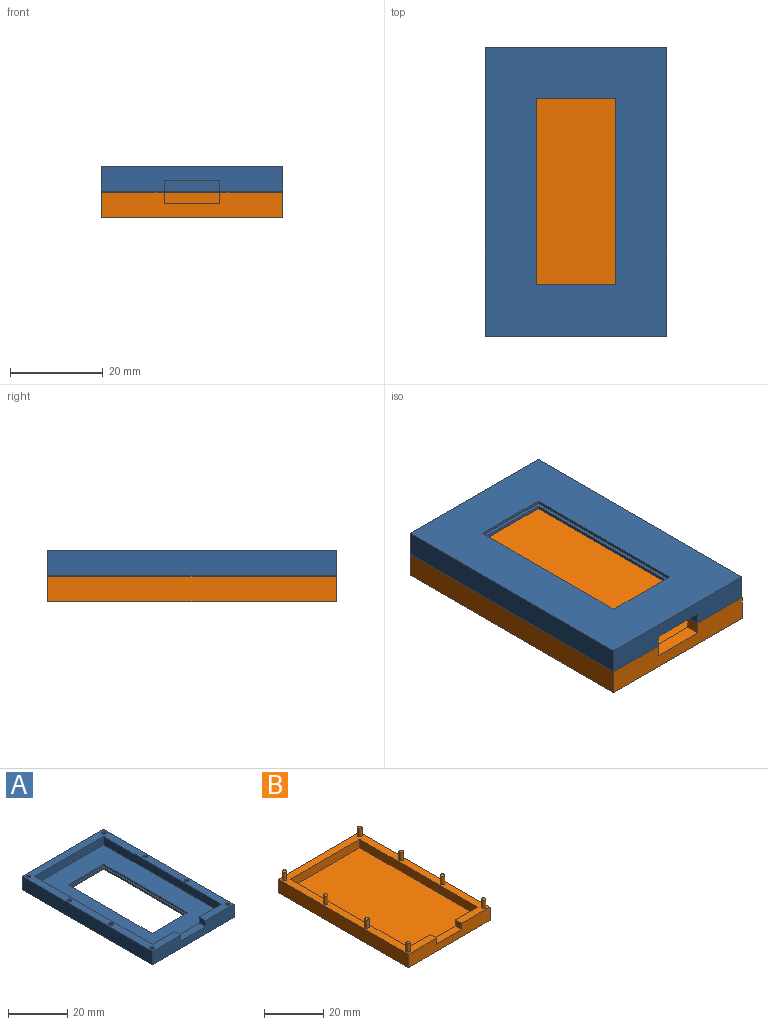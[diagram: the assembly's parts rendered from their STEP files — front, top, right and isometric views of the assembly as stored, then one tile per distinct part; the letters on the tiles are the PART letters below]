
ASSEMBLY  parts=2 mates=1
PART A: 44 faces, bbox 39x62x5.5 mm
  f0: plane 21x0.67mm, normal (0,-1,0), area 14mm2, adj f1,f3,f38,f43
  f1: plane 44x0.67mm, normal (-1,0,0), area 29.3mm2, adj f0,f2,f38,f43
  f2: plane 21x0.67mm, normal (0,1,0), area 14mm2, adj f1,f3,f38,f43
  f3: plane 44x0.67mm, normal (1,0,0), area 29.3mm2, adj f0,f2,f38,f43
  f4: plane 56x33mm, normal (0,0,1), area 1168mm2, adj f6,f7,f8,f9,f39,f40,f41,f42
  f5: plane 62x39mm, normal (0,0,-1), area 1738mm2, adj f12,f13,f14,f15,f34,f35,f36,f37
  f6: plane 33x3.5mm, normal (0,1,0), area 85.5mm2, adj f4,f7,f9,f10,f11,f16,f17
  f7: plane 56x3.5mm, normal (-1,0,0), area 196mm2, adj f4,f6,f8,f16
  f8: plane 33x3.5mm, normal (0,-1,0), area 115.5mm2, adj f4,f7,f9,f16
  f9: plane 56x3.5mm, normal (1,0,0), area 196mm2, adj f4,f6,f8,f16
  f10: plane 3x2.5mm, normal (1,0,0), area 7.5mm2, adj f6,f12,f16,f17
  f11: plane 3x2.5mm, normal (-1,0,0), area 7.5mm2, adj f6,f12,f16,f17
  f12: plane 39x5.5mm, normal (0,-1,0), area 184.5mm2, adj f5,f10,f11,f13,f15,f16,f17
  f13: plane 62x5.5mm, normal (1,0,0), area 341mm2, adj f5,f12,f14,f16
  f14: plane 39x5.5mm, normal (0,1,0), area 214.5mm2, adj f5,f13,f15,f16
  f15: plane 62x5.5mm, normal (-1,0,0), area 341mm2, adj f5,f12,f14,f16
  f16: plane 62x39mm, normal (0,0,1), area 519.9mm2, adj f6,f7,f8,f9,f10,f11,f12,f13
  f17: plane 12x3mm, normal (0,0,1), area 36mm2, adj f6,f10,f11,f12
  f18: cylinder r=0.75mm len=3.35mm, axis (0,0,1), area 15.8mm2, adj f16,f19
  f19: plane 1.5x1.5mm, normal (0,0,1), area 1.8mm2, adj f18
  f20: cylinder r=0.75mm len=3.35mm, axis (0,0,1), area 15.8mm2, adj f16,f21
  f21: plane 1.5x1.5mm, normal (0,0,1), area 1.8mm2, adj f20
  f22: cylinder r=0.75mm len=3.35mm, axis (0,0,1), area 15.8mm2, adj f16,f23
  f23: plane 1.5x1.5mm, normal (0,0,1), area 1.8mm2, adj f22
  f24: cylinder r=0.75mm len=3.35mm, axis (0,0,1), area 15.8mm2, adj f16,f25
  f25: plane 1.5x1.5mm, normal (0,0,1), area 1.8mm2, adj f24
  f26: cylinder r=0.75mm len=3.35mm, axis (0,0,1), area 15.8mm2, adj f16,f27
  f27: plane 1.5x1.5mm, normal (0,0,1), area 1.8mm2, adj f26
  f28: cylinder r=0.75mm len=3.35mm, axis (0,0,1), area 15.8mm2, adj f16,f29
  f29: plane 1.5x1.5mm, normal (0,0,1), area 1.8mm2, adj f28
  f30: cylinder r=0.75mm len=3.35mm, axis (0,0,1), area 15.8mm2, adj f16,f31
  f31: plane 1.5x1.5mm, normal (0,0,1), area 1.8mm2, adj f30
  f32: cylinder r=0.75mm len=3.35mm, axis (0,0,1), area 15.8mm2, adj f16,f33
  f33: plane 1.5x1.5mm, normal (0,0,1), area 1.8mm2, adj f32
  f34: plane 17x0.67mm, normal (0,-1,0), area 11.3mm2, adj f5,f35,f37,f38
  f35: plane 40x0.67mm, normal (-1,0,0), area 26.7mm2, adj f5,f34,f36,f38
  f36: plane 17x0.67mm, normal (0,1,0), area 11.3mm2, adj f5,f35,f37,f38
  f37: plane 40x0.67mm, normal (1,0,0), area 26.7mm2, adj f5,f34,f36,f38
  f38: plane 44x21mm, normal (0,0,1), area 244mm2, adj f0,f1,f2,f3,f34,f35,f36,f37
  f39: plane 17x0.67mm, normal (0,-1,0), area 11.3mm2, adj f4,f40,f42,f43
  f40: plane 40x0.67mm, normal (-1,0,0), area 26.7mm2, adj f4,f39,f41,f43
  f41: plane 17x0.67mm, normal (0,1,0), area 11.3mm2, adj f4,f40,f42,f43
  f42: plane 40x0.67mm, normal (1,0,0), area 26.7mm2, adj f4,f39,f41,f43
  f43: plane 44x21mm, normal (0,0,-1), area 244mm2, adj f0,f1,f2,f3,f39,f40,f41,f42
PART B: 30 faces, bbox 39x62x8.9 mm
  f0: plane 56x33mm, normal (0,0,1), area 1848mm2, adj f2,f3,f4,f5
  f1: plane 62x39mm, normal (0,0,-1), area 2418mm2, adj f8,f9,f10,f11
  f2: plane 33x3.5mm, normal (0,1,0), area 85.5mm2, adj f0,f3,f5,f6,f7,f12,f13
  f3: plane 56x3.5mm, normal (-1,0,0), area 196mm2, adj f0,f2,f4,f12
  f4: plane 33x3.5mm, normal (0,-1,0), area 115.5mm2, adj f0,f3,f5,f12
  f5: plane 56x3.5mm, normal (1,0,0), area 196mm2, adj f0,f2,f4,f12
  f6: plane 3x2.5mm, normal (1,0,0), area 7.5mm2, adj f2,f8,f12,f13
  f7: plane 3x2.5mm, normal (-1,0,0), area 7.5mm2, adj f2,f8,f12,f13
  f8: plane 39x5.5mm, normal (0,-1,0), area 184.5mm2, adj f1,f6,f7,f9,f11,f12,f13
  f9: plane 62x5.5mm, normal (1,0,0), area 341mm2, adj f1,f8,f10,f12
  f10: plane 39x5.5mm, normal (0,1,0), area 214.5mm2, adj f1,f9,f11,f12
  f11: plane 62x5.5mm, normal (-1,0,0), area 341mm2, adj f1,f8,f10,f12
  f12: plane 62x39mm, normal (0,0,1), area 519.9mm2, adj f2,f3,f4,f5,f6,f7,f8,f9
  f13: plane 12x3mm, normal (0,0,1), area 36mm2, adj f2,f6,f7,f8
  f14: cylinder r=0.75mm len=3.35mm, axis (0,0,-1), area 15.8mm2, adj f12,f15
  f15: plane 1.5x1.5mm, normal (0,0,1), area 1.8mm2, adj f14
  f16: cylinder r=0.75mm len=3.35mm, axis (0,0,-1), area 15.8mm2, adj f12,f17
  f17: plane 1.5x1.5mm, normal (0,0,1), area 1.8mm2, adj f16
  f18: cylinder r=0.75mm len=3.35mm, axis (0,0,-1), area 15.8mm2, adj f12,f19
  f19: plane 1.5x1.5mm, normal (0,0,1), area 1.8mm2, adj f18
  f20: cylinder r=0.75mm len=3.35mm, axis (0,0,-1), area 15.8mm2, adj f12,f21
  f21: plane 1.5x1.5mm, normal (0,0,1), area 1.8mm2, adj f20
  f22: cylinder r=0.75mm len=3.35mm, axis (0,0,-1), area 15.8mm2, adj f12,f23
  f23: plane 1.5x1.5mm, normal (0,0,1), area 1.8mm2, adj f22
  f24: cylinder r=0.75mm len=3.35mm, axis (0,0,-1), area 15.8mm2, adj f12,f25
  f25: plane 1.5x1.5mm, normal (0,0,1), area 1.8mm2, adj f24
  f26: cylinder r=0.75mm len=3.35mm, axis (0,0,-1), area 15.8mm2, adj f12,f27
  f27: plane 1.5x1.5mm, normal (0,0,1), area 1.8mm2, adj f26
  f28: cylinder r=0.75mm len=3.35mm, axis (0,0,-1), area 15.8mm2, adj f12,f29
  f29: plane 1.5x1.5mm, normal (0,0,1), area 1.8mm2, adj f28
PLACE A rot(axis=(0,1,0),180deg) t=(0,0,11)mm
PLACE B at identity
MATE planar A.f26 <-> B.f20  axis (0,0,-1) through (-18,-29.5,5.5)mm
